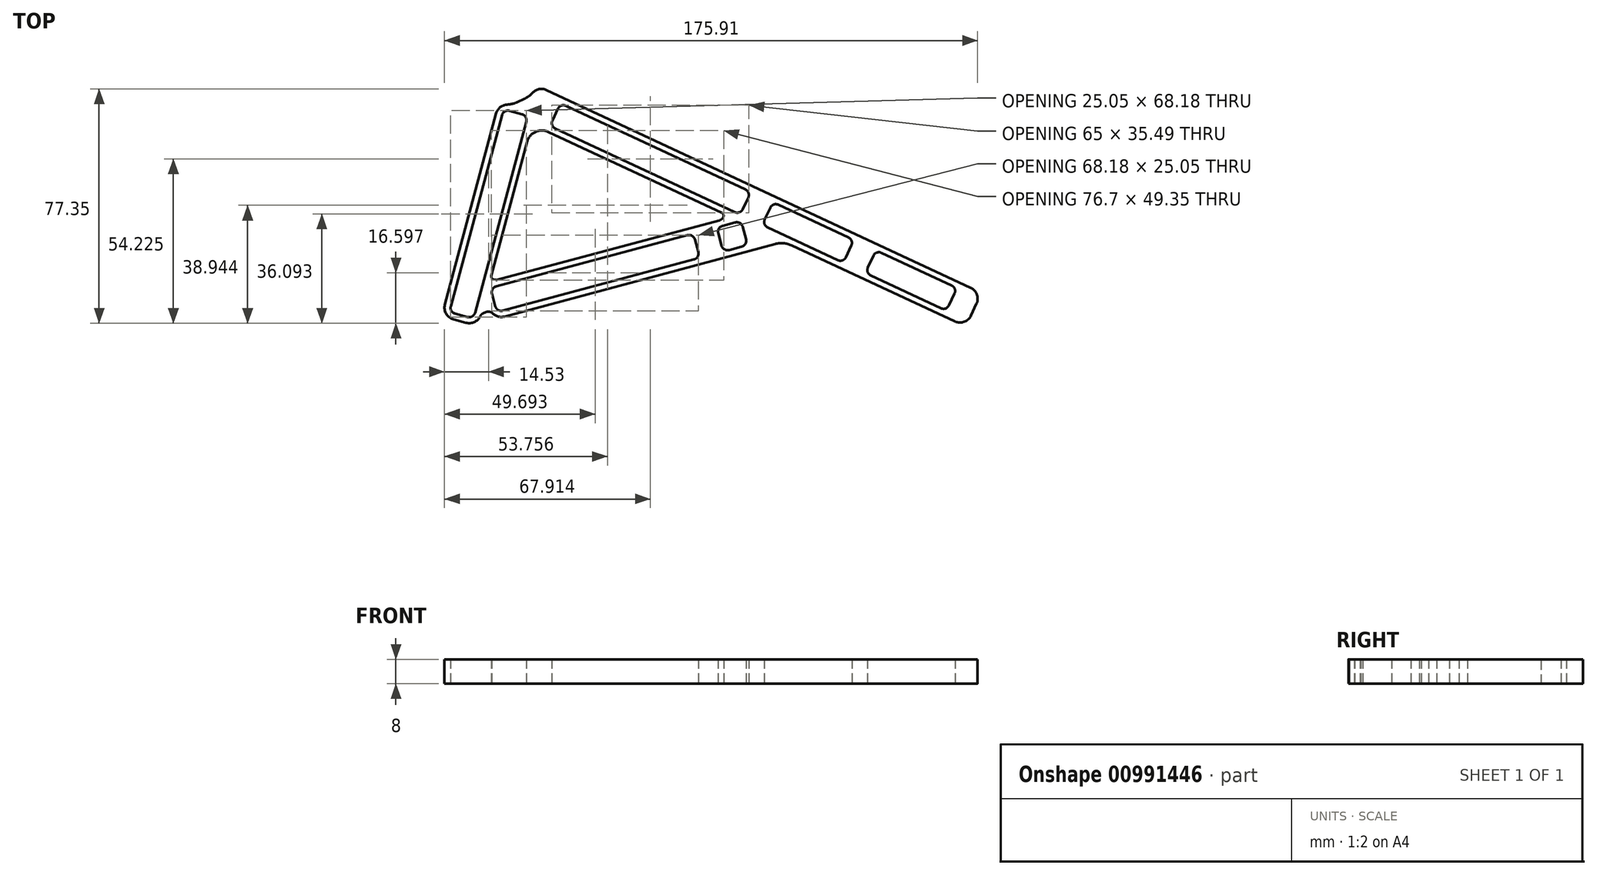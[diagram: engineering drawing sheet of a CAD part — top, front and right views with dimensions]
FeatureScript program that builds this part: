
annotation { "Feature Type Name" : "Feature", "Feature Type Description" : "" }
export const myFeature = defineFeature(function(context is Context, id is Id, definition is map)
    precondition{}
    {
        {
            var Q0;
            Q0=qCreatedBy(makeId("Top.planeOp"),FACE);
            var sketch = newSketch(context, id + "F0", { "sketchPlane" : qUnion([Q0])});
            skLineSegment(sketch, "E0", {"start": v(-115.14, 0) * mm, "end": v(161.49, 0) * mm, "construction": true});
            skLineSegment(sketch, "E1", {"start": v(0.52, 1.93) * mm, "end": v(17.42, 65) * mm});
            skLineSegment(sketch, "E2", {"start": v(17.94, 66.94) * mm, "end": v(122.02, 18.4) * mm, "construction": true});
            skLineSegment(sketch, "E3", {"start": v(0, 0) * mm, "end": v(102.56, 27.48) * mm, "construction": true});
            skLineSegment(sketch, "E4", {"start": v(16, 67.46) * mm, "end": v(11.85, 68.57) * mm});
            skLineSegment(sketch, "E5", {"start": v(9.4, 67.16) * mm, "end": v(-7.5, 4.08) * mm});
            skLineSegment(sketch, "E6", {"start": v(-6.09, 1.63) * mm, "end": v(-1.93, 0.52) * mm});
            skPoint(sketch, "E7.visualSharp", {"position": v(9.92, 69.09) * mm});
            skArc(sketch, "E7.filletArc", {"start": v(11.85, 68.57) * mm, "mid": v(10.33, 68.37) * mm, "end": v(9.4, 67.16) * mm});
            skPoint(sketch, "E8.visualSharp", {"position": v(17.94, 66.94) * mm});
            skArc(sketch, "E8.filletArc", {"start": v(17.42, 65) * mm, "mid": v(17.22, 66.52) * mm, "end": v(16, 67.46) * mm});
            skPoint(sketch, "E9.visualSharp", {"position": v(0, 0) * mm});
            skArc(sketch, "E9.filletArc", {"start": v(-1.93, 0.52) * mm, "mid": v(-0.41, 0.72) * mm, "end": v(0.52, 1.93) * mm});
            skPoint(sketch, "E10.visualSharp", {"position": v(-8.02, 2.15) * mm});
            skArc(sketch, "E10.filletArc", {"start": v(-7.5, 4.08) * mm, "mid": v(-7.3, 2.56) * mm, "end": v(-6.09, 1.63) * mm});
            skArc(sketch, "E11.0", {"start": v(11.18, 70.63) * mm, "mid": v(8.84, 69.76) * mm, "end": v(7.47, 67.67) * mm});
            skLineSegment(sketch, "E11.1", {"start": v(16.52, 69.39) * mm, "end": v(12.37, 70.5) * mm, "construction": true});
            skLineSegment(sketch, "E11.2", {"start": v(7.47, 67.67) * mm, "end": v(-9.43, 4.6) * mm});
            skArc(sketch, "E11.3", {"start": v(19.35, 64.49) * mm, "mid": v(18.95, 67.52) * mm, "end": v(16.52, 69.39) * mm, "construction": true});
            skArc(sketch, "E11.4", {"start": v(-9.43, 4.6) * mm, "mid": v(-9.03, 1.56) * mm, "end": v(-6.6, -0.3) * mm});
            skLineSegment(sketch, "E11.5", {"start": v(-6.6, -0.3) * mm, "end": v(-2.45, -1.41) * mm});
            skArc(sketch, "E11.6", {"start": v(-2.45, -1.41) * mm, "mid": v(0.27, -1.18) * mm, "end": v(2.2, 0.75) * mm});
            skLineSegment(sketch, "E11.7", {"start": v(2.45, 1.41) * mm, "end": v(3.9, 6.8) * mm, "construction": true});
            skLineSegment(sketch, "E12", {"start": v(17.94, 66.94) * mm, "end": v(21.44, 74.46) * mm, "construction": true});
            skLineSegment(sketch, "E13", {"start": v(21.44, 74.46) * mm, "end": v(125.53, 25.93) * mm, "construction": true});
            skLineSegment(sketch, "E14", {"start": v(165, 7.52) * mm, "end": v(161.49, 0) * mm});
            skLineSegment(sketch, "E15", {"start": v(26.03, 65.37) * mm, "end": v(27.85, 69.27) * mm});
            skLineSegment(sketch, "E16", {"start": v(88.84, 36.08) * mm, "end": v(90.66, 39.98) * mm});
            skLineSegment(sketch, "E17.0", {"start": v(24.1, 75.43) * mm, "end": v(164.03, 10.18) * mm});
            skLineSegment(sketch, "E17.1", {"start": v(15.97, 67.46) * mm, "end": v(18.79, 73.5) * mm, "construction": true});
            skLineSegment(sketch, "E17.2", {"start": v(105, 24.13) * mm, "end": v(158.83, -0.97) * mm, "construction": true});
            skLineSegment(sketch, "E17.3", {"start": v(165.96, 4.86) * mm, "end": v(164.14, 0.97) * mm});
            skLineSegment(sketch, "E18", {"start": v(30.5, 70.23) * mm, "end": v(89.69, 42.64) * mm});
            skLineSegment(sketch, "E19", {"start": v(86.18, 35.12) * mm, "end": v(27, 62.71) * mm});
            skPoint(sketch, "E20.visualSharp", {"position": v(28.7, 71.08) * mm});
            skArc(sketch, "E20.filletArc", {"start": v(30.5, 70.23) * mm, "mid": v(28.98, 70.3) * mm, "end": v(27.85, 69.27) * mm});
            skPoint(sketch, "E21.visualSharp", {"position": v(25.19, 63.56) * mm});
            skArc(sketch, "E21.filletArc", {"start": v(26.03, 65.37) * mm, "mid": v(25.97, 63.84) * mm, "end": v(27, 62.71) * mm});
            skPoint(sketch, "E22.visualSharp", {"position": v(88, 34.27) * mm});
            skArc(sketch, "E22.filletArc", {"start": v(86.18, 35.12) * mm, "mid": v(87.71, 35.05) * mm, "end": v(88.84, 36.08) * mm});
            skPoint(sketch, "E23.visualSharp", {"position": v(91.5, 41.8) * mm});
            skArc(sketch, "E23.filletArc", {"start": v(90.66, 39.98) * mm, "mid": v(90.72, 41.5) * mm, "end": v(89.69, 42.64) * mm});
            skPoint(sketch, "E24.visualSharp", {"position": v(20.48, 77.12) * mm});
            skArc(sketch, "E24.filletArc", {"start": v(24.1, 75.43) * mm, "mid": v(21.62, 75.72) * mm, "end": v(19.45, 74.5) * mm});
            skPoint(sketch, "E25.visualSharp", {"position": v(167.65, 8.49) * mm});
            skArc(sketch, "E25.filletArc", {"start": v(165.96, 4.86) * mm, "mid": v(166.1, 7.92) * mm, "end": v(164.03, 10.18) * mm});
            skPoint(sketch, "E26.visualSharp", {"position": v(162.45, -2.66) * mm});
            skArc(sketch, "E26.filletArc", {"start": v(158.83, -0.97) * mm, "mid": v(161.89, -1.1) * mm, "end": v(164.14, 0.97) * mm});
            skLineSegment(sketch, "E27", {"start": v(14.25, 71.38) * mm, "end": v(16.9, 72.62) * mm});
            skPoint(sketch, "E28.visualSharp", {"position": v(12.37, 70.5) * mm});
            skArc(sketch, "E28.filletArc", {"start": v(11.18, 70.63) * mm, "mid": v(12.75, 70.85) * mm, "end": v(14.25, 71.38) * mm});
            skPoint(sketch, "E29.visualSharp", {"position": v(18.79, 73.5) * mm});
            skArc(sketch, "E29.filletArc", {"start": v(16.9, 72.62) * mm, "mid": v(18.27, 73.43) * mm, "end": v(19.45, 74.5) * mm});
            skLineSegment(sketch, "E30", {"start": v(5.87, 14.17) * mm, "end": v(19.25, 64.12) * mm});
            skLineSegment(sketch, "E31", {"start": v(19.25, 64.12) * mm, "end": v(81.96, 34.88) * mm});
            skLineSegment(sketch, "E32", {"start": v(97.9, 36.6) * mm, "end": v(96.09, 32.7) * mm});
            skLineSegment(sketch, "E33", {"start": v(97.06, 30.04) * mm, "end": v(120.2, 19.25) * mm});
            skLineSegment(sketch, "E34", {"start": v(156.9, 4.35) * mm, "end": v(158.71, 8.25) * mm});
            skLineSegment(sketch, "E35", {"start": v(157.74, 10.9) * mm, "end": v(134.6, 21.7) * mm});
            skPoint(sketch, "E36.visualSharp", {"position": v(98.75, 38.41) * mm});
            skArc(sketch, "E36.filletArc", {"start": v(100.56, 37.57) * mm, "mid": v(99.04, 37.63) * mm, "end": v(97.9, 36.6) * mm});
            skPoint(sketch, "E37.visualSharp", {"position": v(95.24, 30.89) * mm});
            skArc(sketch, "E37.filletArc", {"start": v(96.09, 32.7) * mm, "mid": v(96.02, 31.17) * mm, "end": v(97.06, 30.04) * mm});
            skPoint(sketch, "E38.visualSharp", {"position": v(156.05, 2.54) * mm});
            skArc(sketch, "E38.filletArc", {"start": v(154.24, 3.38) * mm, "mid": v(155.77, 3.31) * mm, "end": v(156.9, 4.35) * mm});
            skPoint(sketch, "E39.visualSharp", {"position": v(159.56, 10.06) * mm});
            skArc(sketch, "E39.filletArc", {"start": v(158.71, 8.25) * mm, "mid": v(158.78, 9.77) * mm, "end": v(157.74, 10.9) * mm});
            skLineSegment(sketch, "E40", {"start": v(7.2, 4) * mm, "end": v(6.1, 8.16) * mm});
            skLineSegment(sketch, "E41", {"start": v(7.51, 10.6) * mm, "end": v(70.59, 27.5) * mm});
            skLineSegment(sketch, "E42", {"start": v(73.04, 26.1) * mm, "end": v(74.15, 21.94) * mm});
            skLineSegment(sketch, "E43", {"start": v(72.73, 19.49) * mm, "end": v(9.66, 2.59) * mm});
            skPoint(sketch, "E44.visualSharp", {"position": v(5.58, 10.09) * mm});
            skArc(sketch, "E44.filletArc", {"start": v(7.51, 10.6) * mm, "mid": v(6.3, 9.67) * mm, "end": v(6.1, 8.16) * mm});
            skPoint(sketch, "E45.visualSharp", {"position": v(7.73, 2.07) * mm});
            skArc(sketch, "E45.filletArc", {"start": v(7.2, 4) * mm, "mid": v(8.14, 2.79) * mm, "end": v(9.66, 2.59) * mm});
            skPoint(sketch, "E46.visualSharp", {"position": v(74.67, 20) * mm});
            skArc(sketch, "E46.filletArc", {"start": v(72.73, 19.49) * mm, "mid": v(73.95, 20.42) * mm, "end": v(74.15, 21.94) * mm});
            skPoint(sketch, "E47.visualSharp", {"position": v(72.52, 28.02) * mm});
            skArc(sketch, "E47.filletArc", {"start": v(73.04, 26.1) * mm, "mid": v(72.1, 27.3) * mm, "end": v(70.59, 27.5) * mm});
            skLineSegment(sketch, "E48.2", {"start": v(7.8, 12.75) * mm, "end": v(81.12, 32.4) * mm});
            skArc(sketch, "E48.3", {"start": v(6.31, 1.7) * mm, "mid": v(8.1, 0.66) * mm, "end": v(10.18, 0.66) * mm});
            skLineSegment(sketch, "E48.7", {"start": v(73.56, 17.64) * mm, "end": v(10.18, 0.66) * mm});
            skLineSegment(sketch, "E49", {"start": v(3.24, 1.75) * mm, "end": v(4.12, 2.12) * mm});
            skPoint(sketch, "E50.visualSharp", {"position": v(5.56, 2.73) * mm});
            skArc(sketch, "E50.filletArc", {"start": v(6.31, 1.7) * mm, "mid": v(5.28, 2.24) * mm, "end": v(4.12, 2.12) * mm});
            skPoint(sketch, "E51.visualSharp", {"position": v(2.45, 1.41) * mm});
            skArc(sketch, "E51.filletArc", {"start": v(3.24, 1.75) * mm, "mid": v(2.63, 1.35) * mm, "end": v(2.2, 0.75) * mm});
            skLineSegment(sketch, "E52.trimOffspring", {"start": v(5.6, 13.2) * mm, "end": v(19.35, 64.49) * mm, "construction": true});
            skLineSegment(sketch, "E53", {"start": v(7.28, 12.75) * mm, "end": v(6.57, 12.94) * mm});
            skPoint(sketch, "E54.visualSharp", {"position": v(5.6, 13.2) * mm});
            skArc(sketch, "E54.filletArc", {"start": v(5.87, 14.17) * mm, "mid": v(5.97, 13.4) * mm, "end": v(6.57, 12.94) * mm});
            skPoint(sketch, "E55.visualSharp", {"position": v(7.54, 12.68) * mm});
            skArc(sketch, "E55.filletArc", {"start": v(7.28, 12.75) * mm, "mid": v(7.54, 12.72) * mm, "end": v(7.8, 12.75) * mm});
            skLineSegment(sketch, "E56", {"start": v(73.56, 17.64) * mm, "end": v(99.56, 24.6) * mm});
            skLineSegment(sketch, "E57", {"start": v(80.76, 28.16) * mm, "end": v(81.88, 24) * mm});
            skLineSegment(sketch, "E58", {"start": v(84.33, 22.6) * mm, "end": v(88.48, 23.7) * mm});
            skLineSegment(sketch, "E59", {"start": v(89.9, 26.16) * mm, "end": v(88.78, 30.31) * mm});
            skLineSegment(sketch, "E60", {"start": v(86.33, 31.73) * mm, "end": v(82.18, 30.61) * mm});
            skPoint(sketch, "E61.visualSharp", {"position": v(80.25, 30.1) * mm});
            skArc(sketch, "E61.filletArc", {"start": v(82.18, 30.61) * mm, "mid": v(80.96, 29.68) * mm, "end": v(80.76, 28.16) * mm});
            skArc(sketch, "E62.filletArc", {"start": v(88.78, 30.31) * mm, "mid": v(87.85, 31.53) * mm, "end": v(86.33, 31.73) * mm});
            skPoint(sketch, "E63.visualSharp", {"position": v(90.41, 24.23) * mm});
            skArc(sketch, "E63.filletArc", {"start": v(88.48, 23.7) * mm, "mid": v(89.7, 24.64) * mm, "end": v(89.9, 26.16) * mm});
            skPoint(sketch, "E64.visualSharp", {"position": v(82.4, 22.08) * mm});
            skArc(sketch, "E64.filletArc", {"start": v(81.88, 24) * mm, "mid": v(82.8, 22.8) * mm, "end": v(84.33, 22.6) * mm});
            skPoint(sketch, "E65.newPointB", {"position": v(17.41, 64.98) * mm});
            skArc(sketch, "E65.filletArc", {"start": v(105, 24.13) * mm, "mid": v(102.33, 24.85) * mm, "end": v(99.56, 24.6) * mm});
            skLineSegment(sketch, "E66", {"start": v(82.45, 33.55) * mm, "end": v(82.42, 33.49) * mm});
            skPoint(sketch, "E67.visualSharp", {"position": v(82.02, 32.64) * mm});
            skArc(sketch, "E67.filletArc", {"start": v(81.12, 32.4) * mm, "mid": v(81.89, 32.8) * mm, "end": v(82.42, 33.49) * mm});
            skLineSegment(sketch, "E68.trimOffspring", {"start": v(105, 24.13) * mm, "end": v(158.83, -0.97) * mm});
            skPoint(sketch, "E69.visualSharp", {"position": v(82.87, 34.45) * mm});
            skArc(sketch, "E69.filletArc", {"start": v(82.45, 33.55) * mm, "mid": v(82.48, 34.31) * mm, "end": v(81.96, 34.88) * mm});
            skLineSegment(sketch, "E70", {"start": v(131.93, 20.73) * mm, "end": v(130.12, 16.83) * mm});
            skLineSegment(sketch, "E71", {"start": v(124.68, 24.11) * mm, "end": v(122.87, 20.22) * mm});
            skLineSegment(sketch, "E72", {"start": v(157.8, 6.3) * mm, "end": v(131.03, 18.78) * mm, "construction": true});
            skLineSegment(sketch, "E73", {"start": v(123.78, 22.16) * mm, "end": v(97, 34.65) * mm, "construction": true});
            skLineSegment(sketch, "E74.trimOffspring", {"start": v(129.27, 15.02) * mm, "end": v(161.49, 0) * mm, "construction": true});
            skLineSegment(sketch, "E75.trimOffspring", {"start": v(131.08, 14.18) * mm, "end": v(154.24, 3.38) * mm});
            skLineSegment(sketch, "E76.trimOffspring", {"start": v(132.78, 22.54) * mm, "end": v(165, 7.52) * mm, "construction": true});
            skLineSegment(sketch, "E77.trimOffspring", {"start": v(123.72, 26.77) * mm, "end": v(100.56, 37.57) * mm});
            skPoint(sketch, "E78.visualSharp", {"position": v(125.53, 25.93) * mm});
            skArc(sketch, "E78.filletArc", {"start": v(124.68, 24.11) * mm, "mid": v(124.75, 25.64) * mm, "end": v(123.72, 26.77) * mm});
            skPoint(sketch, "E79.visualSharp", {"position": v(122.02, 18.4) * mm});
            skArc(sketch, "E79.filletArc", {"start": v(120.2, 19.25) * mm, "mid": v(121.74, 19.18) * mm, "end": v(122.87, 20.22) * mm});
            skPoint(sketch, "E80.visualSharp", {"position": v(129.27, 15.02) * mm});
            skArc(sketch, "E80.filletArc", {"start": v(130.12, 16.83) * mm, "mid": v(130.05, 15.3) * mm, "end": v(131.08, 14.18) * mm});
            skPoint(sketch, "E81.visualSharp", {"position": v(132.78, 22.54) * mm});
            skArc(sketch, "E81.filletArc", {"start": v(134.6, 21.7) * mm, "mid": v(133.06, 21.77) * mm, "end": v(131.93, 20.73) * mm});
            skSolve(sketch);
        }
        {
            var Q0;
            Q0=makeQuery(id+"F0.imprint","IMPRINT",FACE,{"disambiguationData":[TD([[makeQuery(id+"F0.imprint","IMPRINT",EDGE,{"derivedFrom":sQuery(id+"F0.wireOp",EDGE,"E1")}),-1.0]])]});
            extrude(context, id + "F1", {"entities" : qUnion([Q0]), "depth" : 8 * mm, "offsetDistance" : 25 * mm});
        }
        {
            var Q0;
            Q0=makeQuery(id+"F1.opExtrude","SWEPT_EDGE",EDGE,{"disambiguationData":[OSD([sQuery(id+"F0.wireOp",EDGE,"E30"),sQuery(id+"F0.wireOp",EDGE,"E31")])]});
            fillet(context, id + "F2", {"entities" : qUnion([Q0]), "radius" : 5 * mm, "tangentPropagation" : true, "allowEdgeOverflow" : false});
        }
    });
